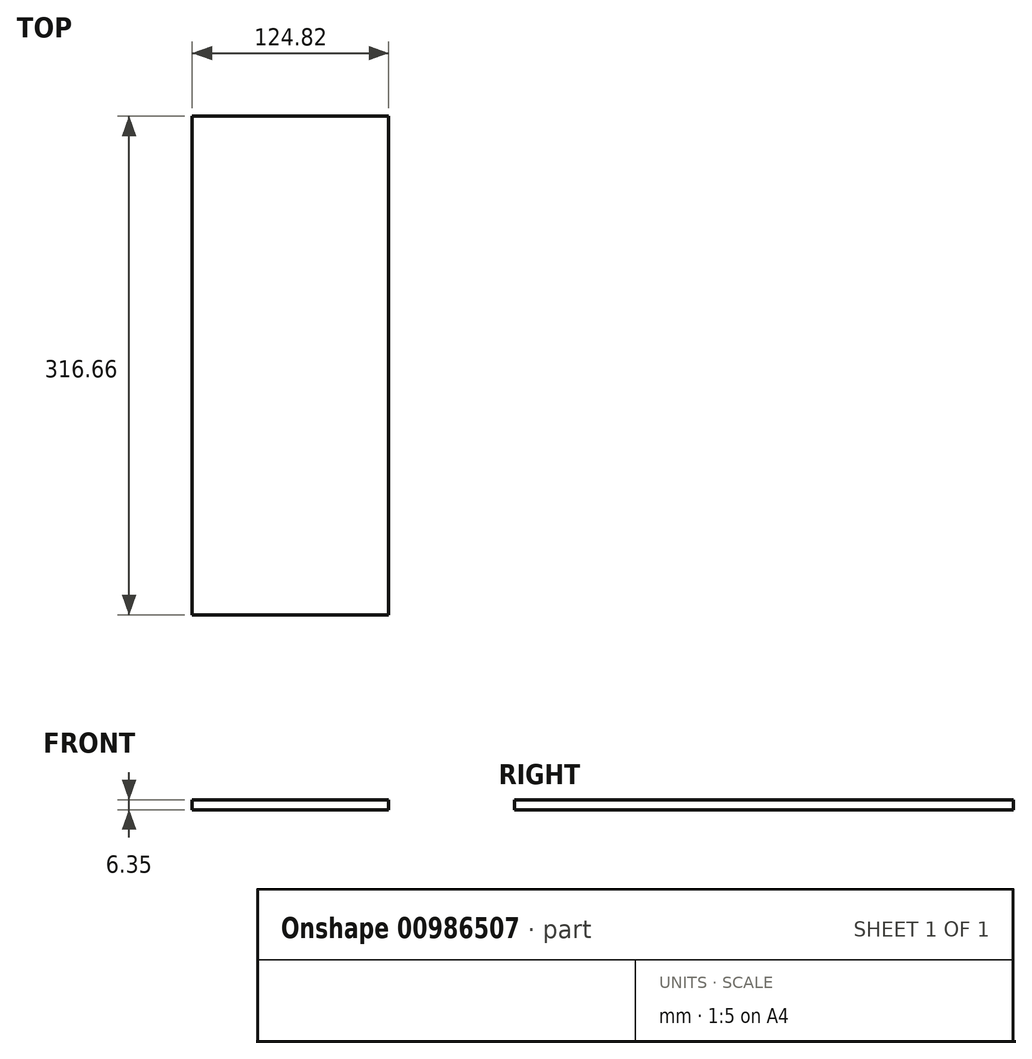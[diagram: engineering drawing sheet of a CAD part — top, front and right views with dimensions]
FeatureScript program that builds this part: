
annotation { "Feature Type Name" : "Feature", "Feature Type Description" : "" }
export const myFeature = defineFeature(function(context is Context, id is Id, definition is map)
    precondition{}
    {
        {
            var Q0;
            Q0=qCreatedBy(makeId("Top.planeOp"),FACE);
            var sketch = newSketch(context, id + "F0", { "sketchPlane" : qUnion([Q0])});
            skLineSegment(sketch, "E0.bottom", {"start": v(62.41, -158.33) * mm, "end": v(-62.41, -158.33) * mm});
            skLineSegment(sketch, "E0.top", {"start": v(62.41, 158.33) * mm, "end": v(-62.41, 158.33) * mm});
            skLineSegment(sketch, "E0.left", {"start": v(62.41, -158.33) * mm, "end": v(62.41, 158.33) * mm});
            skLineSegment(sketch, "E0.right", {"start": v(-62.41, -158.33) * mm, "end": v(-62.41, 158.33) * mm});
            skPoint(sketch, "E0.middle", {"position": v(0, 0) * mm});
            skSolve(sketch);
        }
        {
            var Q0;
            Q0=makeQuery(id+"F0.imprint","IMPRINT",FACE,{"disambiguationData":[TD([[makeQuery(id+"F0.imprint","IMPRINT",EDGE,{"derivedFrom":sQuery(id+"F0.wireOp",EDGE,"E0.bottom")}),-1.0]])]});
            extrude(context, id + "F1", {"entities" : qUnion([Q0]), "oppositeDirection" : true, "depth" : 6.35 * mm, "offsetDistance" : 25.4 * mm});
        }
    });
